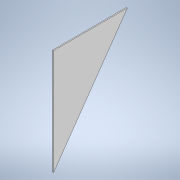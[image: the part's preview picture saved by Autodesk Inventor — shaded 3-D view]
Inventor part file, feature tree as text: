
AUTODESK INVENTOR PART (.ipt)
format: ipt  version: 2021 (Build 250183000, 183)  size: 91,648 bytes
history: native  units: in
note: dims shown in document units (in); Inventor stores cm internally (conversion verified against a paired STEP export)
features: extrude x1, sketch x1
ambient origin geometry x8: Origin, YZ Plane, XZ Plane, XY Plane, X Axis, Y Axis, Z Axis, Center Point
bodies: Solid1 (feature_tree)
feature tree (2):
  extrude  "Extrusion1"  Depth=0.125in
  sketch  "Sketch1"  dims[d0=13.25in d1=9.25in d2=0.125in d3=0.0in]
